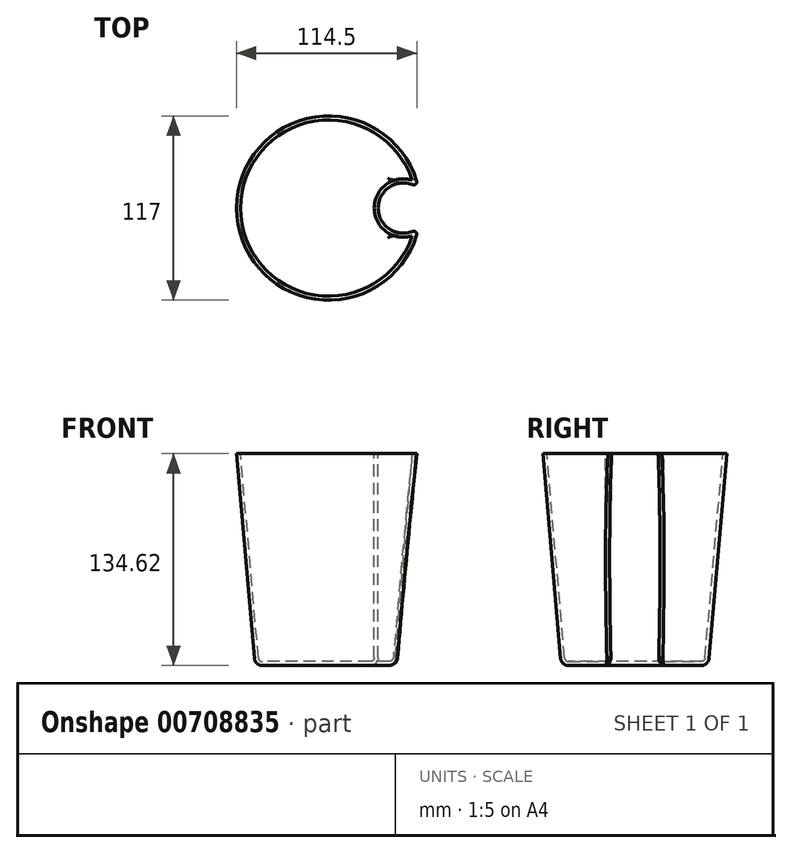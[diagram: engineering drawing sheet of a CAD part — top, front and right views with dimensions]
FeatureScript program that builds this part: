
annotation { "Feature Type Name" : "Feature", "Feature Type Description" : "" }
export const myFeature = defineFeature(function(context is Context, id is Id, definition is map)
    precondition{}
    {
        {
            var Q0;
            Q0=qCreatedBy(makeId("Top.planeOp"),FACE);
            var sketch = newSketch(context, id + "F0", { "sketchPlane" : qUnion([Q0])});
            skCircle(sketch, "E0", {"center": v(0, 0) * mm, "radius": 58.5 * mm});
            skSolve(sketch);
        }
        {
            var Q0;
            Q0 = qSketchRegion(id + "F0", true);
            extrude(context, id + "F1", {"entities" : qUnion([Q0]), "oppositeDirection" : true, "depth" : 134.62 * mm, "offsetDistance" : 25.4 * mm, "hasDraft" : true, "draftAngle" : 5 * degree, "draftPullDirection" : true});
        }
        {
            var Q0;
            Q0=qCreatedBy(makeId("Top.planeOp"),FACE);
            var sketch = newSketch(context, id + "F2", { "sketchPlane" : qUnion([Q0])});
            skCircle(sketch, "E1", {"center": v(47.5, 0) * mm, "radius": 16 * mm});
            skSolve(sketch);
        }
        {
            var Q0;
            Q0=makeQuery(id+"F2.imprint","IMPRINT",FACE,{"disambiguationData":[TD([[makeQuery(id+"F2.imprint","IMPRINT",EDGE,{"derivedFrom":sQuery(id+"F2.wireOp",EDGE,"E1")}),1.0]])]});
            extrude(context, id + "F3", {"entities" : qUnion([Q0]), "operationType" : NewBodyOperationType.REMOVE, "endBound" : BoundingType.THROUGH_ALL, "oppositeDirection" : true, "depth" : 25.4 * mm, "offsetDistance" : 25.4 * mm});
        }
        {
            var Q0;
            Q0=makeQuery(id+"F3.boolean.opBoolean","INTERSECT",EDGE,{"disambiguationData":[OD(0.0)],"derivedFrom":[makeQuery(id+"F1.opExtrude","SWEPT_FACE",FACE,{"disambiguationData":[OSD([sQuery(id+"F0.wireOp",EDGE,"E0")])]}),makeQuery(id+"F3.opExtrude","SWEPT_FACE",FACE,{"disambiguationData":[OSD([sQuery(id+"F2.wireOp",EDGE,"E1")])]})]});
            var Q1;
            Q1=makeQuery(id+"F3.boolean.opBoolean","INTERSECT",EDGE,{"disambiguationData":[OD(1.0)],"derivedFrom":[makeQuery(id+"F1.opExtrude","SWEPT_FACE",FACE,{"disambiguationData":[OSD([sQuery(id+"F0.wireOp",EDGE,"E0")])]}),makeQuery(id+"F3.opExtrude","SWEPT_FACE",FACE,{"disambiguationData":[OSD([sQuery(id+"F2.wireOp",EDGE,"E1")])]})]});
            fillet(context, id + "F4", {"entities" : qUnion([Q0, Q1]), "radius" : 1.9 * mm, "tangentPropagation" : true, "allowEdgeOverflow" : false});
        }
        {
            var Q0;
            Q0=makeQuery(id+"F1.opExtrude","CAP_EDGE",EDGE,{"disambiguationData":[OSD([sQuery(id+"F0.wireOp",EDGE,"E0")])],"isStart":false});
            fillet(context, id + "F5", {"entities" : qUnion([Q0]), "radius" : 5.08 * mm, "tangentPropagation" : true, "allowEdgeOverflow" : false});
        }
        {
            var Q0;
            Q0=makeQuery(id+"F1.opExtrude","CAP_FACE",FACE,{"disambiguationData":[OSD([sQuery(id+"F0.wireOp",EDGE,"E0")])],"isStart":true});
            shell(context, id + "F6", {"entities" : qUnion([Q0]), "thickness" : 2.54 * mm});
        }
    });
